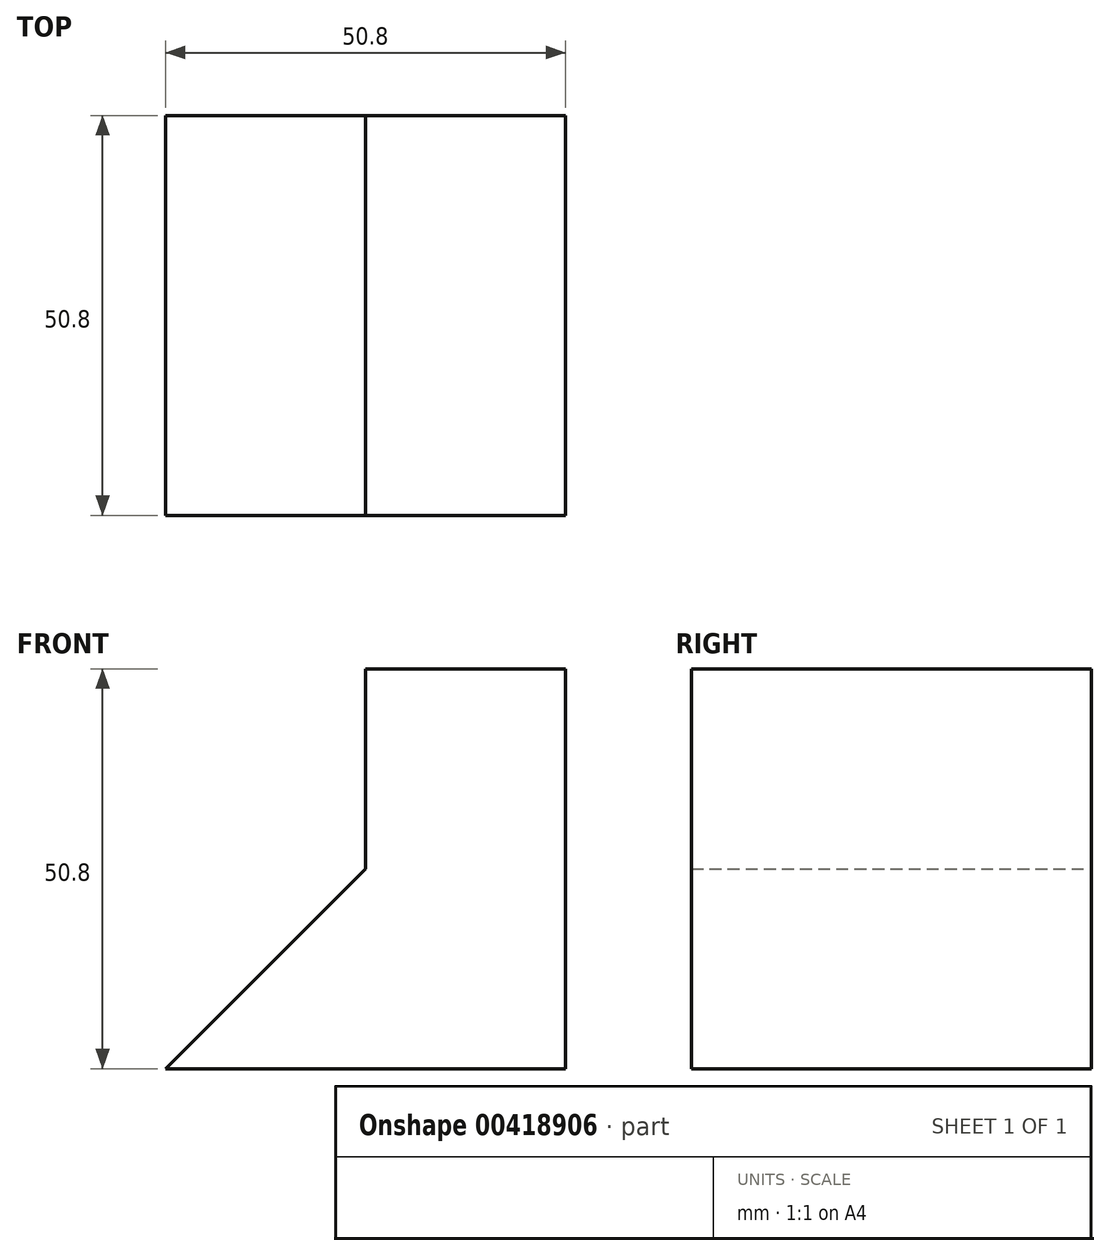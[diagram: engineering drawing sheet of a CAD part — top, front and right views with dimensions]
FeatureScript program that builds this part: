
annotation { "Feature Type Name" : "Feature", "Feature Type Description" : "" }
export const myFeature = defineFeature(function(context is Context, id is Id, definition is map)
    precondition{}
    {
        {
            var Q0;
            Q0=qCreatedBy(makeId("Front.planeOp"),FACE);
            var sketch = newSketch(context, id + "F0", { "sketchPlane" : qUnion([Q0])});
            skLineSegment(sketch, "E0", {"start": v(0, 0) * mm, "end": v(50.8, 0) * mm});
            skLineSegment(sketch, "E1", {"start": v(50.8, 0) * mm, "end": v(50.8, 50.8) * mm});
            skLineSegment(sketch, "E2", {"start": v(50.8, 50.8) * mm, "end": v(25.4, 50.8) * mm});
            skLineSegment(sketch, "E3", {"start": v(25.4, 50.8) * mm, "end": v(25.4, 25.4) * mm});
            skLineSegment(sketch, "E4", {"start": v(25.4, 25.4) * mm, "end": v(0, 0) * mm});
            skSolve(sketch);
        }
        {
            var Q0;
            Q0 = qSketchRegion(id + "F0", true);
            extrude(context, id + "F1", {"entities" : qUnion([Q0]), "depth" : 50.8 * mm});
        }
    });
